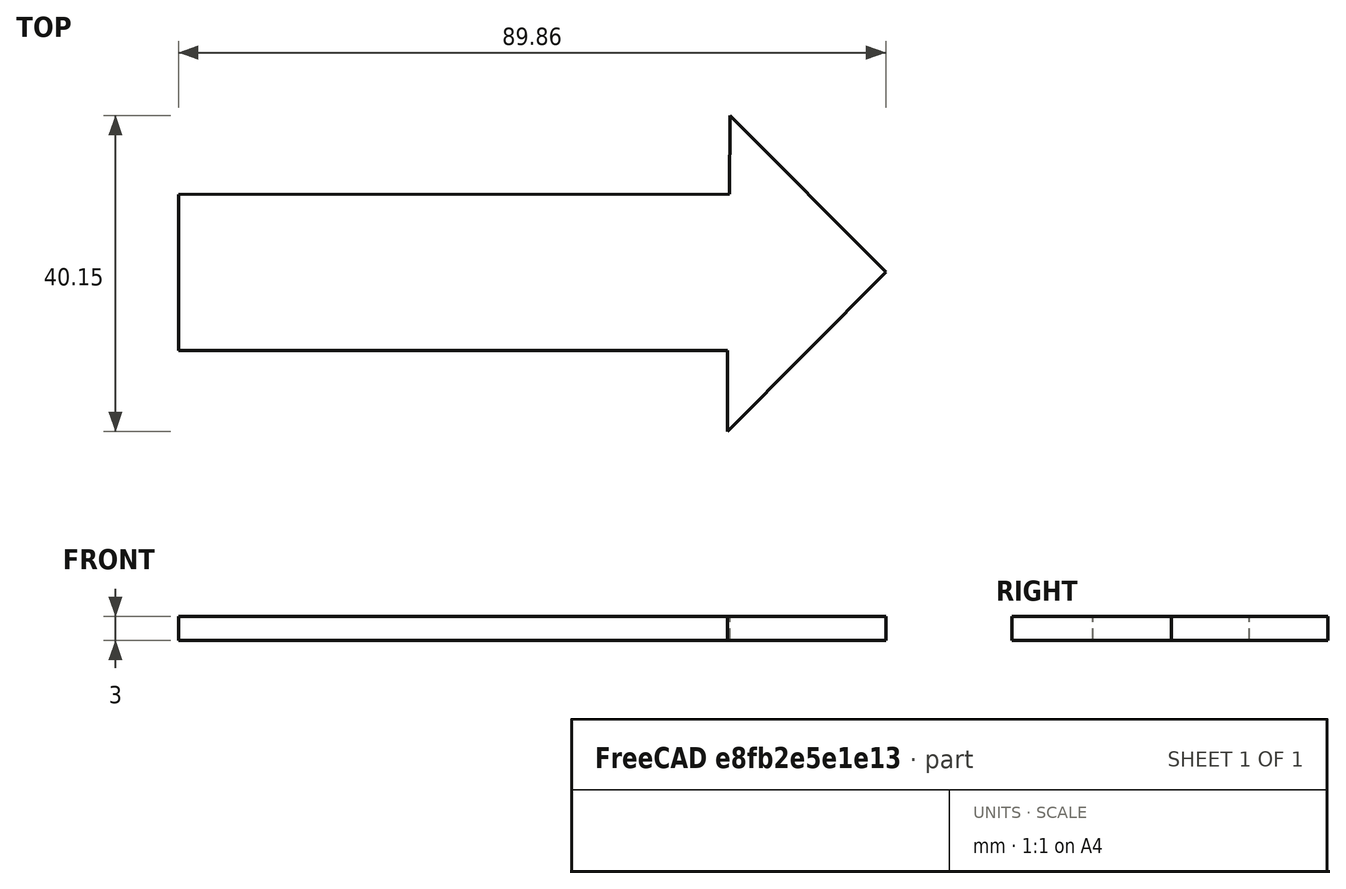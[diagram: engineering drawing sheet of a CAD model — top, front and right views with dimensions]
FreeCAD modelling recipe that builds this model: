
FCSTD DOCUMENT  (FreeCAD 0.21R33771 (Git))
Label: OJT1_T16R02_fletxa
License: All rights reserved
LicenseURL: http://en.wikipedia.org/wiki/All_rights_reserved
objects: Sketcher::SketchObject×1, PartDesign::Pad×1, PartDesign::Body×1
note: 4 computed .brp shape members not serialized (recipe doc carries the construction recipe); baked Part::Feature solids carry a one-line shape summary decoded from their .brp

FEATURE [Sketcher::SketchObject] Sketch
  FullyConstrained = false
  MapMode = 5
  Support = -> [XY_Plane]
  sketch-geometry (7):
    g0: LineSegment StartX=-29.9315 StartY=9.86301 StartZ=0 EndX=40.0598 EndY=9.90058 EndZ=0
    g1: LineSegment StartX=40.0598 StartY=9.90058 StartZ=0 EndX=40.0685 EndY=19.863 EndZ=0
    g2: LineSegment StartX=40.0685 StartY=19.863 StartZ=0 EndX=59.8939 EndY=-0.016484 EndZ=0
    g3: LineSegment StartX=59.8939 StartY=-0.016484 StartZ=0 EndX=39.7992 EndY=-20.2894 EndZ=0
    g4: LineSegment StartX=39.7992 StartY=-20.2894 StartZ=0 EndX=39.7992 EndY=-9.9898 EndZ=0
    g5: LineSegment StartX=39.7992 StartY=-9.9898 StartZ=0 EndX=-29.9675 EndY=-9.9898 EndZ=0
    g6: LineSegment StartX=-29.9675 StartY=-9.9898 StartZ=0 EndX=-29.9315 EndY=9.86301 EndZ=0
  constraints (5):
    c: Coincident(g0,g1)
    c: Coincident(g1,g2)
    c: Coincident(g3,g4)
    c: Coincident(g4,g5)
    c: Coincident(g5,g6)
FEATURE [PartDesign::Pad] Pad
  Direction = (0,0,1)
  Length = 3
  Length2 = 10
  Profile = -> Sketch
  ReferenceAxis = -> Sketch [N_Axis]
  Type = 0
FEATURE [PartDesign::Body] Body
  Group = -> [Sketch,Pad]
  Origin = -> Origin
  Tip = -> Pad
